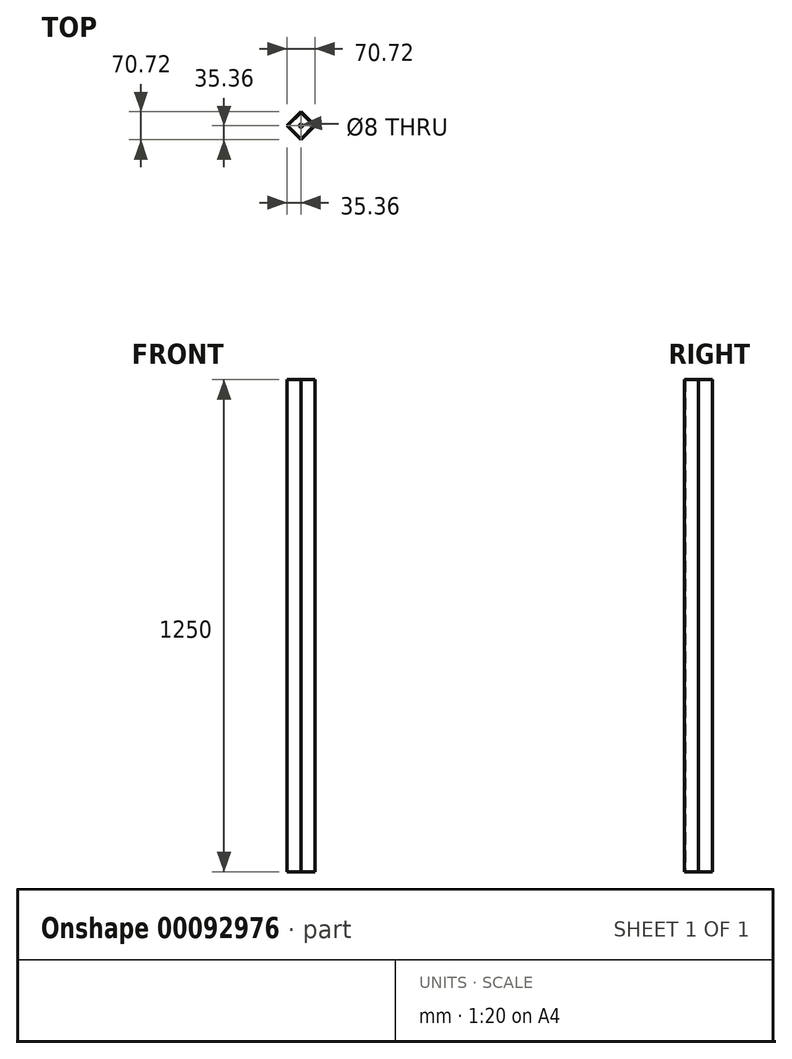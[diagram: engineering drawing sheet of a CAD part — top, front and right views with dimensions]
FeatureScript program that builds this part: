
annotation { "Feature Type Name" : "Feature", "Feature Type Description" : "" }
export const myFeature = defineFeature(function(context is Context, id is Id, definition is map)
    precondition{}
    {
        {
            var Q0;
            Q0=qCreatedBy(makeId("Top.planeOp"),FACE);
            var sketch = newSketch(context, id + "F0", { "sketchPlane" : qUnion([Q0])});
            skLineSegment(sketch, "E0", {"start": v(0, 35.36) * mm, "end": v(35.36, 0) * mm});
            skLineSegment(sketch, "E1", {"start": v(35.36, 0) * mm, "end": v(0, -35.36) * mm});
            skLineSegment(sketch, "E2", {"start": v(0, -35.36) * mm, "end": v(-35.36, 0) * mm});
            skLineSegment(sketch, "E3", {"start": v(-35.36, 0) * mm, "end": v(0, 35.36) * mm});
            skSolve(sketch);
        }
        {
            var Q0;
            Q0=makeQuery(id+"F0.imprint","IMPRINT",FACE,{"disambiguationData":[TD([[makeQuery(id+"F0.imprint","IMPRINT",EDGE,{"derivedFrom":sQuery(id+"F0.wireOp",EDGE,"E0")}),-1.0]])]});
            extrude(context, id + "F1", {"entities" : qUnion([Q0]), "depth" : 1250 * mm});
        }
        {
            var Q0;
            Q0=makeQuery(id+"F1.opExtrude","CAP_FACE",FACE,{"disambiguationData":[OSD([sQuery(id+"F0.wireOp",EDGE,"E0"),sQuery(id+"F0.wireOp",EDGE,"E1"),sQuery(id+"F0.wireOp",EDGE,"E2"),sQuery(id+"F0.wireOp",EDGE,"E3")])],"isStart":false});
            shell(context, id + "F2", {"entities" : qUnion([Q0]), "thickness" : 1.25 * mm});
        }
        {
            var Q0;
            Q0=makeQuery(id+"F1.opExtrude","CAP_FACE",FACE,{"disambiguationData":[OSD([sQuery(id+"F0.wireOp",EDGE,"E0"),sQuery(id+"F0.wireOp",EDGE,"E1"),sQuery(id+"F0.wireOp",EDGE,"E2"),sQuery(id+"F0.wireOp",EDGE,"E3")])],"isStart":true});
            var sketch = newSketch(context, id + "F3", { "sketchPlane" : qUnion([Q0])});
            skCircle(sketch, "E4", {"center": v(0, 0) * mm, "radius": 4 * mm});
            skSolve(sketch);
        }
        {
            var Q0;
            Q0 = qSketchRegion(id + "F3", true);
            extrude(context, id + "F4", {"entities" : qUnion([Q0]), "operationType" : NewBodyOperationType.REMOVE, "endBound" : BoundingType.SYMMETRIC, "oppositeDirection" : true, "depth" : 25 * mm});
        }
    });
